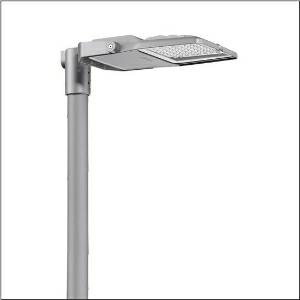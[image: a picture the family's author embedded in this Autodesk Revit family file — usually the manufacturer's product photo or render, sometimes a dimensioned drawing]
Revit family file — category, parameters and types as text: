
# Revit family: floodlight_fl_21_iq_mini___pl43_5xa7772d2a3a_1f0e
name_source: partatom
category: Lighting Fixtures
units: mm (PartAtom-declared; Revit-internal decimal feet)

## family parameters
Cut with Voids When Loaded = No
Host = Face
Light Source = No
Part Type = Normal
Room Calculation Point = No
Round Connector Dimension = Use Diameter
Shared = No

## types (1)
- --- (1 x LED, 18290 lm, 143 W, 3000K)
    Apparent Load = 143 VA
    CIE Flux Codes = 27 78 99 100 100
    Color Rendering = 70
    Color Temperature = 3000K
    Default Elevation = 1800 mm
    Description = Floodlight FL 21 iQ mini, floodlight, primary light control with lens, of PMMA, primary optical cover: protective disc, of toughened safety glass, transparent, light distribution: PL43, light emission: direct distribution, installation type: surface-mounted, LED, High Power LED, rated luminous flux: 18.290lm, luminous efficacy: 128lm/W, light colour: 730, colour temperature: 3000K, control gear: iQ Street-Remote/DALI, control: Auto-Match, Temp-Guard, Night-Set, Smart-Wire, Desk-Remote (wireless, voltage-free reading and setting of iQ features in the workshop via application-optimized NFC function/RFID function), optimised constant luminous flux control (CLO 2.0), Light-Fading, Lumen-Switch, with terminal, 6-pole, mains connection: 220..240V, AC, 50/60Hz, start of lifetime: 143W, end of service life: 152W, reduction: 61W, luminaire housing, of diecast aluminium, powder-coated, Siteco® metallic grey (DB 702S), corrosivity category C5 mid according to DIN EN ISO 12944, suitable for swimming pools, chlorine-resistant, sealing non-destructively replaceable, please order mast flange separately, mast bracket, of steel, galvanised, powder-coated, protection rating (complete): IP66, insulation class (complete): insulation class II (safety insulation), certification: CE, ENEC, VDE, protection symbol: D, impact resistance: IK08, permissible operating ambient temperature: -40..+40°C, permissible operating ambient temperature for outdoor applications: -40..+50°C, standard: DIN EN 12944, LABS conformity tested according to VDMA 24364:2018-05, packaging unit: 1 piece

Light Distribution: PL43
    Height = 70 mm
    Lamp = 1 x LED
    Lamp Light Flux = 18290 lm
    Lamp Power = 143 W
    Lamp count = 1
    Length = 485 mm
    Luminous efficacy = 128 lm/W
    Manufacturer = Siteco
    ModVariant = No
    Model = 5XA7772D2A3A
    Number of Poles = 1
    OnlyDefault = Yes
    Power Factor = 1
    Product Name = Floodlight FL 21 iQ mini | PL43
    Product group = floodlight | pylon annexe
    ProductGroupID = 6200
    Protection Class = Protection class II
    Protection Degree = IP 66
    RLX_Detail_Level = 1
    RLX_Emergency_Light_Flux = 0 lm
    RLX_Emergency_Type = 0
    RLX_Emergency_Type_DB = No
    RlxData = <blob elided: 101465 chars, md5=7eb4b27d>
    Socket = socket
    Standby Power = 0 W
    System Light Flux = 18290 lm
    System Power = 143 W
    Type Comments = factory setting: luminous flux: 100 % | dim-lin: 254 | 730 mA
    Type Image = l_1007125.jpg
    URL = http://relux.com
    VarID = @adj_161624
    Voltage = 0 V
    Weight = 0.00 kg
    Width = 337 mm

## geometry (parser evidence)
native form markers: Blend x4, Sweep x12
no freeform markers — native parametric forms only
